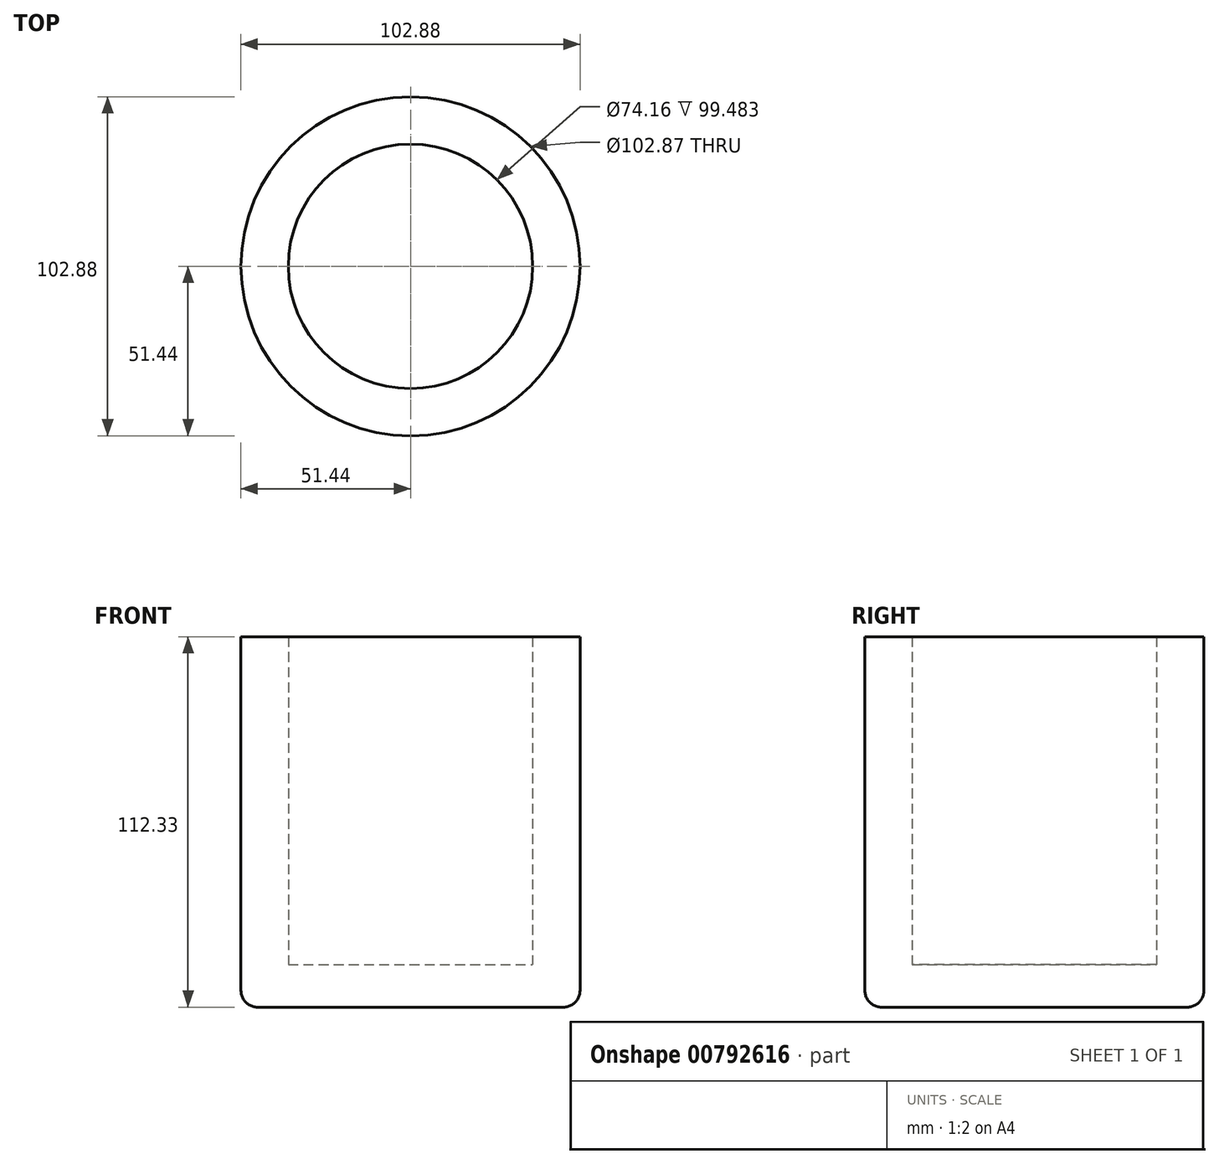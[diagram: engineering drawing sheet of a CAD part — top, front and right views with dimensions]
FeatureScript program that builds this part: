
annotation { "Feature Type Name" : "Feature", "Feature Type Description" : "" }
export const myFeature = defineFeature(function(context is Context, id is Id, definition is map)
    precondition{}
    {
        {
            var Q0;
            Q0=qCreatedBy(makeId("Front.planeOp"),FACE);
            var sketch = newSketch(context, id + "F0", { "sketchPlane" : qUnion([Q0])});
            skLineSegment(sketch, "E0", {"start": v(37.08, 50.65) * mm, "end": v(37.08, -48.83) * mm});
            skLineSegment(sketch, "E1", {"start": v(37.08, -48.83) * mm, "end": v(0, -48.83) * mm});
            skLineSegment(sketch, "E2", {"start": v(51.44, 50.64) * mm, "end": v(51.44, -50.04) * mm});
            skLineSegment(sketch, "E3", {"start": v(51.44, -50.04) * mm, "end": v(51.44, -61.68) * mm});
            skLineSegment(sketch, "E4", {"start": v(51.44, -61.68) * mm, "end": v(0, -61.68) * mm});
            skLineSegment(sketch, "E5", {"start": v(0, 28.27) * mm, "end": v(0, -38.24) * mm});
            skSolve(sketch);
        }
        {
            var Q0;
            Q0 = qSketchRegion(id + "F0", true);
            var Q1;
            Q1=sQuery(id+"F0.wireOp",EDGE,"E0");
            var Q2;
            Q2=sQuery(id+"F0.wireOp",EDGE,"E2");
            var Q3;
            Q3=sQuery(id+"F0.wireOp",EDGE,"E3");
            var Q4;
            Q4=sQuery(id+"F0.wireOp",EDGE,"E4");
            var Q5;
            Q5=sQuery(id+"F0.wireOp",EDGE,"E1");
            var Q6;
            Q6=sQuery(id+"F0.wireOp",EDGE,"E5");
            revolve(context, id + "F1", {"bodyType" : ToolBodyType.SURFACE, "surfaceOperationType" : NewSurfaceOperationType.NEW, "entities" : qUnion([Q0]), "surfaceEntities" : qUnion([Q1, Q2, Q3, Q4, Q5]), "axis" : qUnion([Q6]), "revolveType" : RevolveType.FULL});
        }
        {
            var Q0;
            Q0=makeQuery(id+"F1.opRevolve","SWEPT_FACE",FACE,{"disambiguationData":[OSD([sQuery(id+"F0.wireOp",EDGE,"E2"),sQuery(id+"F0.wireOp",EDGE,"E3")])]});
            fillet(context, id + "F2", {"entities" : qUnion([Q0]), "radius" : 5 * mm, "tangentPropagation" : true, "allowEdgeOverflow" : false});
        }
    });
